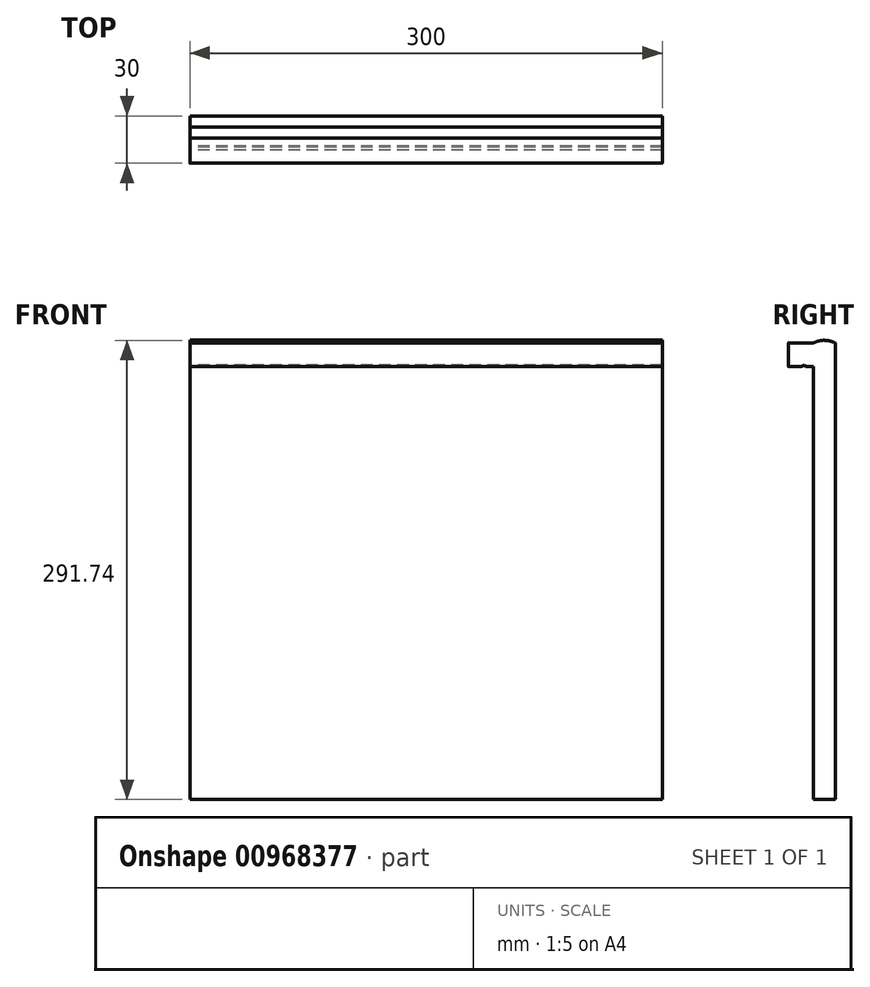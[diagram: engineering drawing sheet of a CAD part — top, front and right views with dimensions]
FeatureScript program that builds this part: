
annotation { "Feature Type Name" : "Feature", "Feature Type Description" : "" }
export const myFeature = defineFeature(function(context is Context, id is Id, definition is map)
    precondition{}
    {
        {
            var Q0;
            Q0=qCreatedBy(makeId("Right.planeOp"),FACE);
            var sketch = newSketch(context, id + "F0", { "sketchPlane" : qUnion([Q0])});
            skLineSegment(sketch, "E0", {"start": v(0, -200.18) * mm, "end": v(14, -200.18) * mm});
            skLineSegment(sketch, "E1", {"start": v(14, -200.18) * mm, "end": v(14, 89.82) * mm});
            skLineSegment(sketch, "E2", {"start": v(0, 89.82) * mm, "end": v(-15.95, 89.82) * mm});
            skLineSegment(sketch, "E3", {"start": v(-16, 89.77) * mm, "end": v(-16, 75.08) * mm});
            skLineSegment(sketch, "E4", {"start": v(-15.75, 74.82) * mm, "end": v(-7.7, 74.82) * mm});
            skLineSegment(sketch, "E5", {"start": v(-7.7, 74.82) * mm, "end": v(-5.74, 75.94) * mm});
            skLineSegment(sketch, "E6", {"start": v(-5.74, 75.94) * mm, "end": v(-5.1, 74.82) * mm});
            skLineSegment(sketch, "E7", {"start": v(-5.1, 74.82) * mm, "end": v(0, 74.82) * mm});
            skPoint(sketch, "E8.visualSharp", {"position": v(-16, 74.82) * mm});
            skArc(sketch, "E8.filletArc", {"start": v(-16, 75.08) * mm, "mid": v(-15.93, 74.9) * mm, "end": v(-15.75, 74.82) * mm});
            skArc(sketch, "E9", {"start": v(6.81, 91.56) * mm, "mid": v(3.3, 91.1) * mm, "end": v(0, 89.82) * mm});
            skArc(sketch, "E10", {"start": v(14, 89.82) * mm, "mid": v(10.5, 91.06) * mm, "end": v(6.81, 91.56) * mm});
            skLineSegment(sketch, "E11", {"start": v(0, 74.82) * mm, "end": v(0, -200.18) * mm});
            skPoint(sketch, "E12.visualSharp", {"position": v(-16, 89.82) * mm});
            skArc(sketch, "E12.filletArc", {"start": v(-15.95, 89.82) * mm, "mid": v(-15.99, 89.8) * mm, "end": v(-16, 89.77) * mm});
            skSolve(sketch);
        }
        {
            var Q0;
            Q0 = qSketchRegion(id + "F0", true);
            extrude(context, id + "F1", {"entities" : qUnion([Q0]), "depth" : 300 * mm, "offsetDistance" : 25 * mm});
        }
    });
